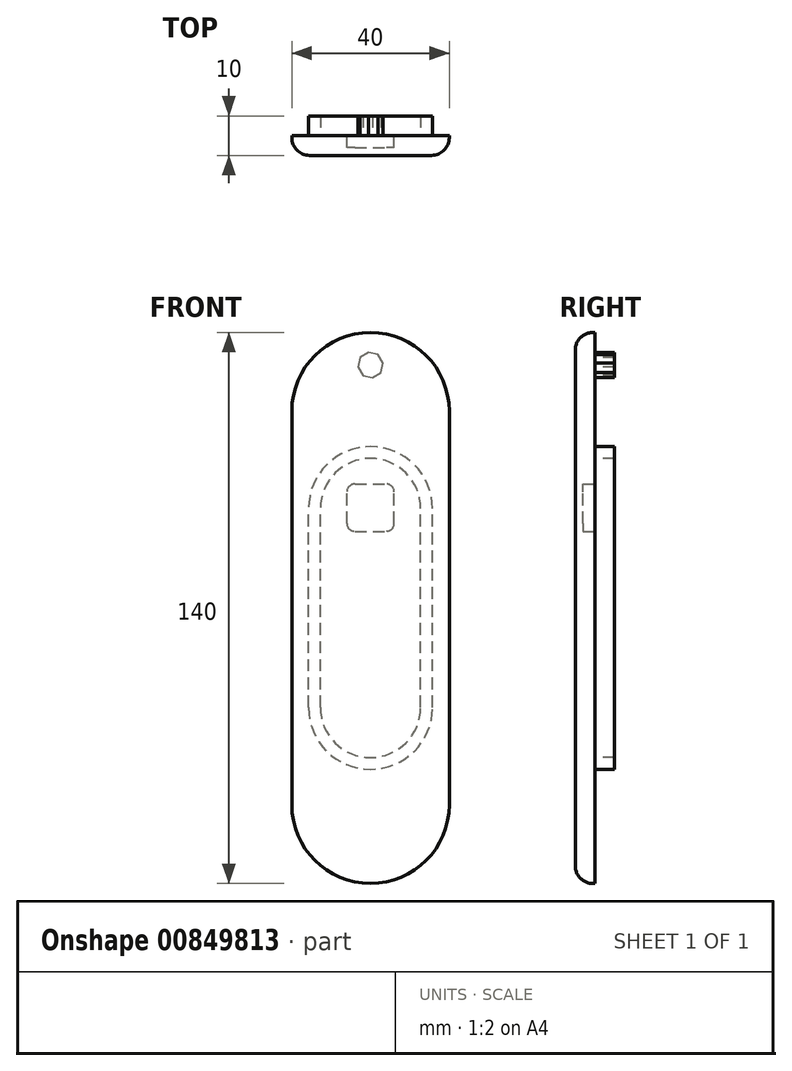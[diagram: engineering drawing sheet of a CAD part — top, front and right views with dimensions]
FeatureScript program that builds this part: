
annotation { "Feature Type Name" : "Feature", "Feature Type Description" : "" }
export const myFeature = defineFeature(function(context is Context, id is Id, definition is map)
    precondition{}
    {
        {
            var Q0;
            Q0=qCreatedBy(makeId("Front.planeOp"),FACE);
            var sketch = newSketch(context, id + "F0", { "sketchPlane" : qUnion([Q0])});
            skLineSegment(sketch, "E0.bottom", {"start": v(20, -70) * mm, "end": v(-20, -70) * mm});
            skLineSegment(sketch, "E0.top", {"start": v(20, 70) * mm, "end": v(-20, 70) * mm});
            skLineSegment(sketch, "E0.left", {"start": v(20, -70) * mm, "end": v(20, 70) * mm});
            skLineSegment(sketch, "E0.right", {"start": v(-20, -70) * mm, "end": v(-20, 70) * mm});
            skPoint(sketch, "E0.middle", {"position": v(0, 0) * mm});
            skSolve(sketch);
        }
        {
            var Q0;
            Q0 = qSketchRegion(id + "F0", true);
            extrude(context, id + "F1", {"entities" : qUnion([Q0]), "depth" : 5 * mm, "offsetDistance" : 25 * mm});
        }
        {
            var Q0;
            Q0=makeQuery(id+"F1.opExtrude","SWEPT_EDGE",EDGE,{"disambiguationData":[OSD([sQuery(id+"F0.wireOp",EDGE,"E0.top"),sQuery(id+"F0.wireOp",EDGE,"E0.right")])]});
            var Q1;
            Q1=makeQuery(id+"F1.opExtrude","SWEPT_EDGE",EDGE,{"disambiguationData":[OSD([sQuery(id+"F0.wireOp",EDGE,"E0.top"),sQuery(id+"F0.wireOp",EDGE,"E0.left")])]});
            var Q2;
            Q2=makeQuery(id+"F1.opExtrude","SWEPT_EDGE",EDGE,{"disambiguationData":[OSD([sQuery(id+"F0.wireOp",EDGE,"E0.bottom"),sQuery(id+"F0.wireOp",EDGE,"E0.left")])]});
            var Q3;
            Q3=makeQuery(id+"F1.opExtrude","SWEPT_EDGE",EDGE,{"disambiguationData":[OSD([sQuery(id+"F0.wireOp",EDGE,"E0.bottom"),sQuery(id+"F0.wireOp",EDGE,"E0.right")])]});
            fillet(context, id + "F2", {"entities" : qUnion([Q0, Q1, Q2, Q3]), "radius" : 20 * mm, "tangentPropagation" : true, "allowEdgeOverflow" : false});
        }
        {
            var Q0;
            Q0=makeQuery(id+"F1.opExtrude","CAP_EDGE",EDGE,{"disambiguationData":[OSD([sQuery(id+"F0.wireOp",EDGE,"E0.left")])],"isStart":false});
            fillet(context, id + "F3", {"entities" : qUnion([Q0]), "radius" : 4.5 * mm, "tangentPropagation" : true, "allowEdgeOverflow" : false});
        }
        {
            var Q0;
            Q0=makeQuery(id+"F1.opExtrude","CAP_FACE",FACE,{"disambiguationData":[OSD([sQuery(id+"F0.wireOp",EDGE,"E0.bottom"),sQuery(id+"F0.wireOp",EDGE,"E0.top"),sQuery(id+"F0.wireOp",EDGE,"E0.left"),sQuery(id+"F0.wireOp",EDGE,"E0.right")])],"isStart":true});
            var sketch = newSketch(context, id + "F4", { "sketchPlane" : qUnion([Q0])});
            skLineSegment(sketch, "E1", {"start": v(0, 0) * mm, "end": v(0, 61.75) * mm, "construction": true});
            skCircle(sketch, "E2", {"center": v(0, 61.75) * mm, "radius": 3 * mm});
            skCircle(sketch, "E3.cCircle", {"center": v(0, 61.75) * mm, "radius": 3 * mm, "construction": true});
            skLineSegment(sketch, "E3.0", {"start": v(3.2, 61.2) * mm, "end": v(1.88, 59.1) * mm});
            skLineSegment(sketch, "E3.1", {"start": v(1.88, 59.1) * mm, "end": v(-0.54, 58.55) * mm});
            skLineSegment(sketch, "E3.2", {"start": v(-0.54, 58.55) * mm, "end": v(-2.65, 59.87) * mm});
            skLineSegment(sketch, "E3.3", {"start": v(-2.65, 59.87) * mm, "end": v(-3.2, 62.3) * mm});
            skLineSegment(sketch, "E3.4", {"start": v(-3.2, 62.3) * mm, "end": v(-1.88, 64.4) * mm});
            skLineSegment(sketch, "E3.5", {"start": v(-1.88, 64.4) * mm, "end": v(0.54, 64.95) * mm});
            skLineSegment(sketch, "E3.6", {"start": v(0.54, 64.95) * mm, "end": v(2.65, 63.63) * mm});
            skLineSegment(sketch, "E3.7", {"start": v(2.65, 63.63) * mm, "end": v(3.2, 61.2) * mm});
            skPoint(sketch, "E3.0.midPoint", {"position": v(2.54, 60.15) * mm});
            skSolve(sketch);
        }
        {
            var Q0;
            Q0 = qSketchRegion(id + "F4", true);
            extrude(context, id + "F5", {"entities" : qUnion([Q0]), "operationType" : NewBodyOperationType.ADD, "depth" : 5 * mm, "offsetDistance" : 25 * mm});
        }
        {
            var Q0;
            Q0=makeQuery(id+"F1.opExtrude","CAP_FACE",FACE,{"disambiguationData":[OSD([sQuery(id+"F0.wireOp",EDGE,"E0.bottom"),sQuery(id+"F0.wireOp",EDGE,"E0.top"),sQuery(id+"F0.wireOp",EDGE,"E0.left"),sQuery(id+"F0.wireOp",EDGE,"E0.right")])],"isStart":true});
            var sketch = newSketch(context, id + "F6", { "sketchPlane" : qUnion([Q0])});
            skLineSegment(sketch, "E4", {"start": v(0, 0) * mm, "end": v(0, 25.5) * mm, "construction": true});
            skLineSegment(sketch, "E5.bottom", {"start": v(6, 19.5) * mm, "end": v(-6, 19.5) * mm});
            skLineSegment(sketch, "E5.top", {"start": v(6, 31.5) * mm, "end": v(-6, 31.5) * mm});
            skLineSegment(sketch, "E5.left", {"start": v(6, 19.5) * mm, "end": v(6, 31.5) * mm});
            skLineSegment(sketch, "E5.right", {"start": v(-6, 19.5) * mm, "end": v(-6, 31.5) * mm});
            skPoint(sketch, "E5.middle", {"position": v(0, 25.5) * mm});
            skSolve(sketch);
        }
        {
            var Q0;
            Q0 = qSketchRegion(id + "F6", true);
            extrude(context, id + "F7", {"entities" : qUnion([Q0]), "operationType" : NewBodyOperationType.REMOVE, "oppositeDirection" : true, "depth" : 3 * mm, "offsetDistance" : 25 * mm});
        }
        {
            var Q0;
            Q0=makeQuery(id+"F7.boolean.opBoolean","COPY",EDGE,{"derivedFrom":makeQuery(id+"F7.opExtrude","SWEPT_EDGE",EDGE,{"disambiguationData":[OSD([sQuery(id+"F6.wireOp",EDGE,"E5.top"),sQuery(id+"F6.wireOp",EDGE,"E5.right")])]})});
            var Q1;
            Q1=makeQuery(id+"F7.boolean.opBoolean","COPY",EDGE,{"derivedFrom":makeQuery(id+"F7.opExtrude","SWEPT_EDGE",EDGE,{"disambiguationData":[OSD([sQuery(id+"F6.wireOp",EDGE,"E5.top"),sQuery(id+"F6.wireOp",EDGE,"E5.left")])]})});
            var Q2;
            Q2=makeQuery(id+"F7.boolean.opBoolean","COPY",EDGE,{"derivedFrom":makeQuery(id+"F7.opExtrude","SWEPT_EDGE",EDGE,{"disambiguationData":[OSD([sQuery(id+"F6.wireOp",EDGE,"E5.bottom"),sQuery(id+"F6.wireOp",EDGE,"E5.left")])]})});
            var Q3;
            Q3=makeQuery(id+"F7.boolean.opBoolean","COPY",EDGE,{"derivedFrom":makeQuery(id+"F7.opExtrude","SWEPT_EDGE",EDGE,{"disambiguationData":[OSD([sQuery(id+"F6.wireOp",EDGE,"E5.bottom"),sQuery(id+"F6.wireOp",EDGE,"E5.right")])]})});
            fillet(context, id + "F8", {"entities" : qUnion([Q0, Q1, Q2, Q3]), "radius" : 2 * mm, "tangentPropagation" : true, "allowEdgeOverflow" : false});
        }
        {
            var Q0;
            Q0=makeQuery(id+"F1.opExtrude","CAP_FACE",FACE,{"disambiguationData":[OSD([sQuery(id+"F0.wireOp",EDGE,"E0.bottom"),sQuery(id+"F0.wireOp",EDGE,"E0.top"),sQuery(id+"F0.wireOp",EDGE,"E0.left"),sQuery(id+"F0.wireOp",EDGE,"E0.right")])],"isStart":true});
            var sketch = newSketch(context, id + "F9", { "sketchPlane" : qUnion([Q0])});
            skLineSegment(sketch, "E6.bottom", {"start": v(0, -41) * mm, "end": v(0, -41) * mm});
            skLineSegment(sketch, "E6.top", {"start": v(0, 41) * mm, "end": v(0, 41) * mm});
            skLineSegment(sketch, "E6.left", {"start": v(15.75, -25.25) * mm, "end": v(15.75, 25.25) * mm});
            skLineSegment(sketch, "E6.right", {"start": v(-15.75, -25.25) * mm, "end": v(-15.75, 25.25) * mm});
            skPoint(sketch, "E6.middle", {"position": v(0, 0) * mm});
            skPoint(sketch, "E7.visualSharp", {"position": v(-15.75, 41) * mm});
            skArc(sketch, "E7.filletArc", {"start": v(0, 41) * mm, "mid": v(-11.14, 36.39) * mm, "end": v(-15.75, 25.25) * mm});
            skPoint(sketch, "E8.visualSharp", {"position": v(15.75, 41) * mm});
            skArc(sketch, "E8.filletArc", {"start": v(15.75, 25.25) * mm, "mid": v(11.14, 36.39) * mm, "end": v(0, 41) * mm});
            skPoint(sketch, "E9.visualSharp", {"position": v(-15.75, -41) * mm});
            skArc(sketch, "E9.filletArc", {"start": v(-15.75, -25.25) * mm, "mid": v(-11.14, -36.39) * mm, "end": v(0, -41) * mm});
            skPoint(sketch, "E10.visualSharp", {"position": v(15.75, -41) * mm});
            skArc(sketch, "E10.filletArc", {"start": v(0, -41) * mm, "mid": v(11.14, -36.39) * mm, "end": v(15.75, -25.25) * mm});
            skArc(sketch, "E11.0", {"start": v(0, -38) * mm, "mid": v(9.02, -34.27) * mm, "end": v(12.75, -25.25) * mm});
            skArc(sketch, "E11.1", {"start": v(12.75, 25.25) * mm, "mid": v(9.02, 34.27) * mm, "end": v(0, 38) * mm});
            skArc(sketch, "E11.2", {"start": v(0, 38) * mm, "mid": v(-9.02, 34.27) * mm, "end": v(-12.75, 25.25) * mm});
            skLineSegment(sketch, "E11.3", {"start": v(12.75, -25.25) * mm, "end": v(12.75, 25.25) * mm});
            skLineSegment(sketch, "E11.4", {"start": v(-12.75, -25.25) * mm, "end": v(-12.75, 25.25) * mm});
            skArc(sketch, "E11.5", {"start": v(-12.75, -25.25) * mm, "mid": v(-9.02, -34.27) * mm, "end": v(0, -38) * mm});
            skSolve(sketch);
        }
        {
            var Q0;
            Q0 = qSketchRegion(id + "F9", true);
            extrude(context, id + "F10", {"entities" : qUnion([Q0]), "operationType" : NewBodyOperationType.ADD, "depth" : 5 * mm, "offsetDistance" : 25 * mm});
        }
    });
